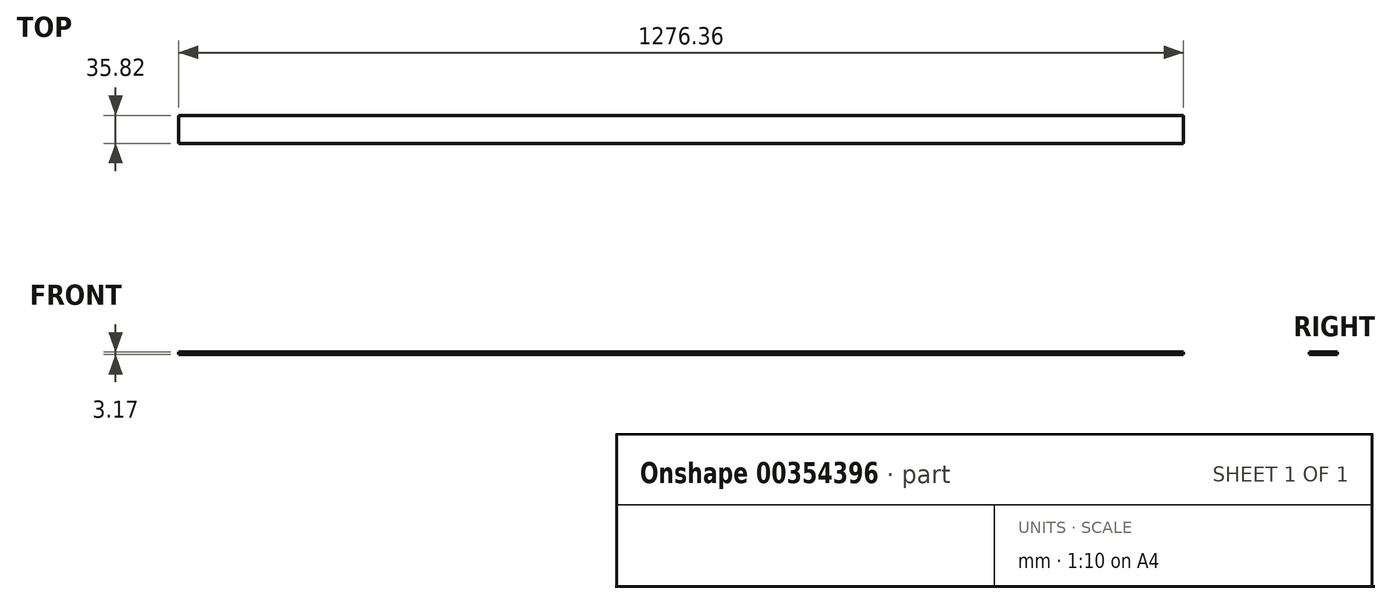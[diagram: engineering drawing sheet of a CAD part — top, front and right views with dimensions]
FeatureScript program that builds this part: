
annotation { "Feature Type Name" : "Feature", "Feature Type Description" : "" }
export const myFeature = defineFeature(function(context is Context, id is Id, definition is map)
    precondition{}
    {
        {
            var Q0;
            Q0=qCreatedBy(makeId("Top.planeOp"),FACE);
            var sketch = newSketch(context, id + "F0", { "sketchPlane" : qUnion([Q0])});
            skLineSegment(sketch, "E0.bottom", {"start": v(638.18, 17.9) * mm, "end": v(-638.18, 17.9) * mm});
            skLineSegment(sketch, "E0.top", {"start": v(638.18, -17.9) * mm, "end": v(-638.18, -17.9) * mm});
            skLineSegment(sketch, "E0.left", {"start": v(638.18, 17.9) * mm, "end": v(638.18, -17.9) * mm});
            skLineSegment(sketch, "E0.right", {"start": v(-638.18, 17.9) * mm, "end": v(-638.18, -17.9) * mm});
            skPoint(sketch, "E0.middle", {"position": v(0, 0) * mm});
            skSolve(sketch);
        }
        {
            var Q0;
            Q0 = qSketchRegion(id + "F0", true);
            extrude(context, id + "F1", {"entities" : qUnion([Q0]), "depth" : 3.17 * mm});
        }
    });
